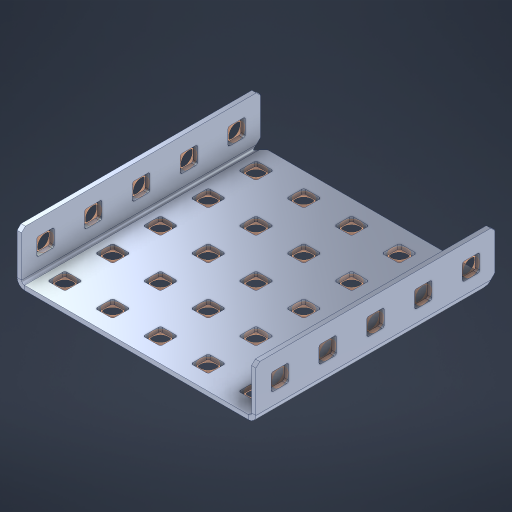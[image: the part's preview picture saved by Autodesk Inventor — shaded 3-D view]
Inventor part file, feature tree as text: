
AUTODESK INVENTOR PART (.ipt)
format: ipt  version: 2023 (Build 270158000, 158)  size: 713,216 bytes
history: native  units: in
note: dims shown in document units (in); Inventor stores cm internally (conversion verified against a paired STEP export)
features: other x40, extrude x34, sheet_metal_op x10, sketch x8, mirror x1, pattern_linear x1, chamfer x1
ambient origin geometry x8: Origin, YZ Plane, XZ Plane, XY Plane, X Axis, Y Axis, Z Axis, Center Point
bodies: Solid1 (feature_tree), Body (feature_tree)
feature tree (95):
  other  "Flange Pattern Plane"
  sheet_metal_op  "Flange Pattern"
  sheet_metal_op  "Body Pattern"
  other  "Arc Length"
  mirror  "Notch Mirror"
  pattern_linear  "Notch Pattern"  Spacing1=0.1875in  [1 undecoded]
  chamfer  "End Chamfer"
  extrude  "Half Cut"  Depth=0.0469in
  sketch  "Sketch1"  dims[d0=2.5in]
  other  "Plate1"
  sketch  "Sketch2"  dims[d1=2.5in]
  other  "Plate2"
  sheet_metal_op  "Bend1"
  sheet_metal_op  "Corner1"
  sketch  "Sketch3"  dims[d2=0.0469in]
  other  "Flange Pattern Sketch"
  sketch  "Sketch7"  dims[d3=0.0469in]
  other  "Srf1"
  other  "Srf2"
  sketch  "Sketch8"  dims[d4=0.0234in]
  sketch  "Sketch9"  dims[d5=0.0938in]
  other  "Srf91"
  sheet_metal_op  "Body Pattern Sketch"
  other  "Srf92"
  sketch  "Sketch13"  dims[d6=0.0469in]
  sketch  "Sketch14"  dims[d7=0.5in d8=90.0deg d9=0.0312in d10=0.1875in d11=0.0469in d12=0.0469in d16=0.182in d17=0.02in d18=0.0469in d19=0.0in d20=0.25in d21=0.25in d46=0.172in d47=1.0in d48=0.0in d49=0.182in d50=0.02in d51=0.25in d52=0.25in d53=0.0469in d54=0.0in d55=0.172in d56=1.0in d57=0.0in d60=1.9685in d62=0.5in d63=1.9685in d65=0.5in d85=0.1227in d86=0.1659in d88=0.04in d89=0.0469in d90=0.0in d91=0.04in d92=0.0491in d95=2.5in d96=0.04in d97=0.25in d98=45.0deg d101=0.0in d102=2.497in d131=2.5in d132=1.9685in d134=0.5in d139=0.5in]
  other  "Srf856"
  other  "Srf1310"
  other  "Srf1311"
  other  "Srf1312"
  other  "Srf1376"
  other  "Srf1377"
  other  "Srf1728"
  other  "Srf1755"
  other  "Srf1878"
  other  "Srf1879"
  other  "Srf1880"
  other  "Srf1881"
  other  "Srf1942"
  other  "Srf1943"
  other  "Srf1944"
  other  "Srf1945"
  other  "Srf1946"
  other  "Srf1947"
  other  "Srf1948"
  other  "Srf1949"
  other  "Srf1950"
  other  "Srf1951"
  other  "Srf1952"
  other  "Srf1953"
  other  "Srf1954"
  other  "Srf1955"
  other  "Srf1956"
  other  "Srf1957"
  other  "Srf1958"
  other  "Srf1959"
  other  "Srf1960"
  sheet_metal_op  "Flange Stamp"
  sheet_metal_op  "Flange Circle"
  sheet_metal_op  "Body Stamp"
  sheet_metal_op  "Body Circle"
  sheet_metal_op  "Notch"
  extrude  "ExtrusionSrf2"  Depth=0.0469in
  extrude  "ExtrusionSrf92"  Depth=2.5in
  extrude  "ExtrusionSrf856"  Depth=0.02in
  extrude  "ExtrusionSrf1310"  Depth=0.0469in
  extrude  "ExtrusionSrf1311"  TaperAngle=0.0deg  [1 undecoded]
  extrude  "ExtrusionSrf1312"  Depth=0.25in
  extrude  "ExtrusionSrf1376"  Depth=0.25in
  extrude  "ExtrusionSrf1377"  Depth=2.5in
  extrude  "ExtrusionSrf1728"  Depth=2.5in TaperAngle=0.0deg
  extrude  "ExtrusionSrf1755"  Depth=2.5in
  extrude  "ExtrusionSrf1878"  Depth=0.02in
  extrude  "ExtrusionSrf1879"  Depth=0.25in
  extrude  "ExtrusionSrf1880"  Depth=0.25in
  extrude  "ExtrusionSrf1881"  Depth=0.0469in
  extrude  "ExtrusionSrf1942"  TaperAngle=0.0deg  [1 undecoded]
  extrude  "ExtrusionSrf1943"  Depth=2.5in
  extrude  "ExtrusionSrf1944"  Depth=2.5in TaperAngle=0.0deg
  extrude  "ExtrusionSrf1945"  Depth=2.5in
  extrude  "ExtrusionSrf1946"  Depth=2.5in
  extrude  "ExtrusionSrf1947"  Depth=2.5in
  extrude  "ExtrusionSrf1948"  Depth=2.5in
  extrude  "ExtrusionSrf1949"  Depth=2.5in
  extrude  "ExtrusionSrf1950"  Depth=0.0469in
  extrude  "ExtrusionSrf1951"  TaperAngle=0.0deg  [1 undecoded]
  extrude  "ExtrusionSrf1952"  Depth=2.5in
  extrude  "ExtrusionSrf1953"  Depth=2.5in
  extrude  "ExtrusionSrf1954"  Depth=2.5in
  extrude  "ExtrusionSrf1955"  Depth=0.25in TaperAngle=45.0deg
  extrude  "ExtrusionSrf1956"  TaperAngle=0.0deg  [1 undecoded]
  extrude  "ExtrusionSrf1957"  Depth=2.5in
  extrude  "ExtrusionSrf1958"  Depth=2.5in
  extrude  "ExtrusionSrf1959"  Depth=2.5in
  extrude  "ExtrusionSrf1960"  Depth=2.5in
note: 5 required parameter values undecoded (feature->parameter linkage not recoverable at this tier; creation-order binding heuristic only, values carry confidence <= 0.55)
